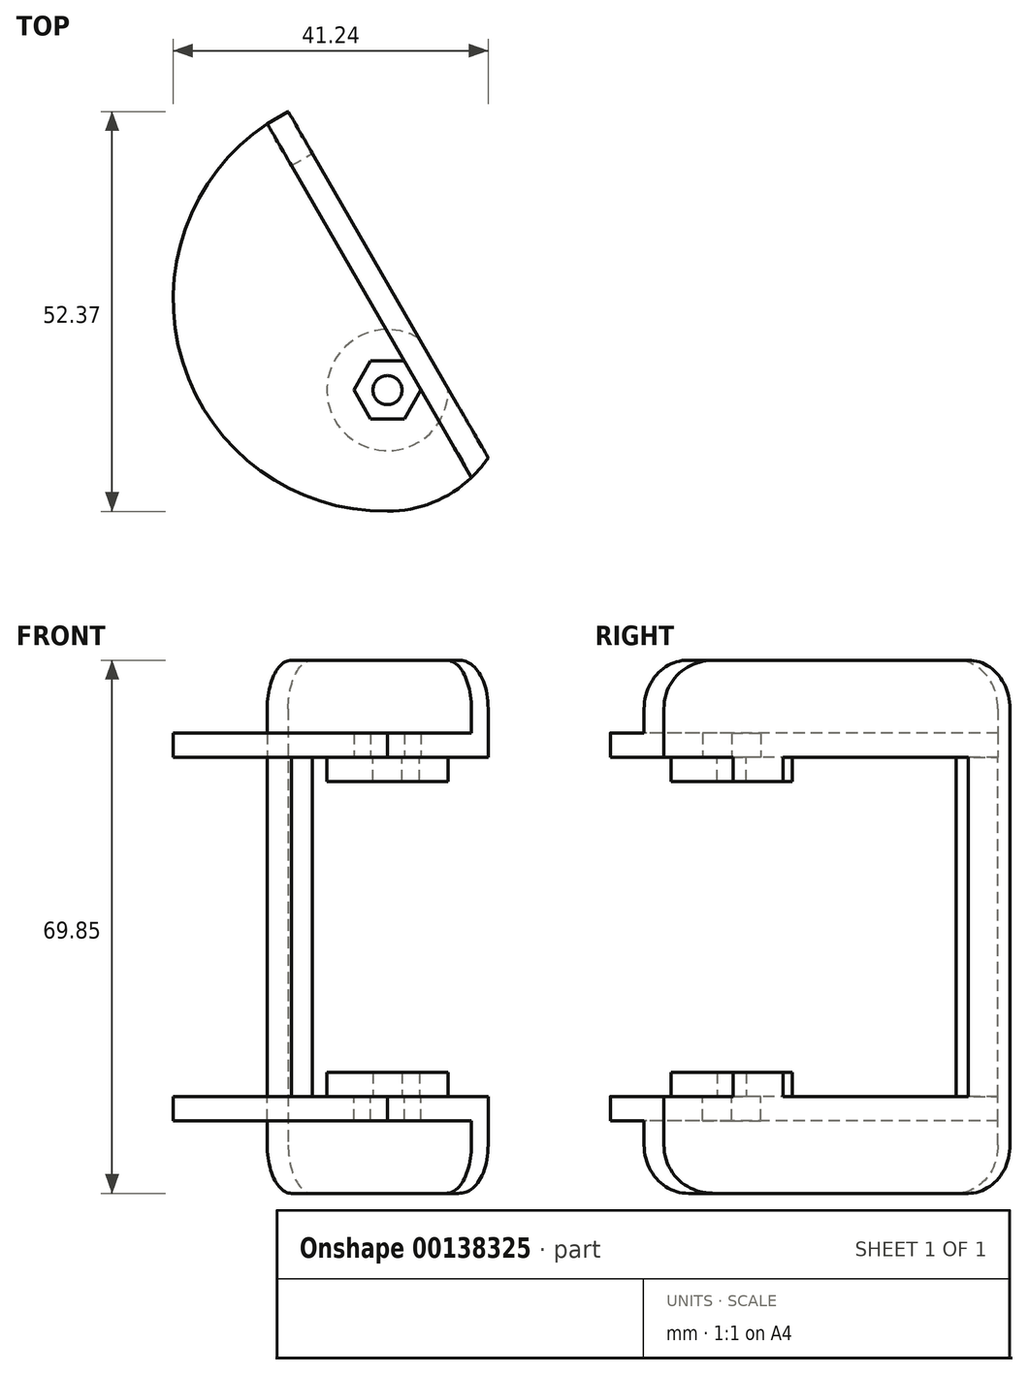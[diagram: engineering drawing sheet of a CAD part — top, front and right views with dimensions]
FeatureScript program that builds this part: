
annotation { "Feature Type Name" : "Feature", "Feature Type Description" : "" }
export const myFeature = defineFeature(function(context is Context, id is Id, definition is map)
    precondition{}
    {
        {
            var Q0;
            Q0=qCreatedBy(makeId("Top.planeOp"),FACE);
            var sketch = newSketch(context, id + "F0", { "sketchPlane" : qUnion([Q0])});
            skArc(sketch, "E0", {"start": v(-4.4, 15.25) * mm, "mid": v(-12.83, -9.36) * mm, "end": v(13.18, -8.85) * mm});
            skPoint(sketch, "E1", {"position": v(0, -15.88) * mm});
            skArc(sketch, "E2", {"start": v(-15.75, 34.9) * mm, "mid": v(-26.82, 3.64) * mm, "end": v(0, -15.88) * mm});
            skCircle(sketch, "E3", {"center": v(0, 0) * mm, "radius": 1.9 * mm});
            skCircle(sketch, "E4.cCircle", {"center": v(0, 0) * mm, "radius": 3.81 * mm, "construction": true});
            skLineSegment(sketch, "E4.0", {"start": v(4.4, 0) * mm, "end": v(2.2, -3.81) * mm});
            skLineSegment(sketch, "E4.1", {"start": v(2.2, -3.81) * mm, "end": v(-2.2, -3.81) * mm});
            skLineSegment(sketch, "E4.2", {"start": v(-2.2, -3.8) * mm, "end": v(-4.4, 0) * mm});
            skLineSegment(sketch, "E4.3", {"start": v(-4.4, 0) * mm, "end": v(-2.2, 3.81) * mm});
            skLineSegment(sketch, "E4.4", {"start": v(-2.2, 3.81) * mm, "end": v(2.2, 3.8) * mm});
            skLineSegment(sketch, "E4.5", {"start": v(2.2, 3.8) * mm, "end": v(4.4, 0) * mm});
            skPoint(sketch, "E4.0.midPoint", {"position": v(3.3, -1.9) * mm});
            skLineSegment(sketch, "E5", {"start": v(11, -11.44) * mm, "end": v(-15.75, 34.9) * mm});
            skLineSegment(sketch, "E6", {"start": v(-15.75, 34.9) * mm, "end": v(-15.75, 34.9) * mm});
            skLineSegment(sketch, "E7", {"start": v(13.18, -8.85) * mm, "end": v(-13, 36.49) * mm});
            skLineSegment(sketch, "E8", {"start": v(-15.75, 34.9) * mm, "end": v(-13, 36.49) * mm});
            skLineSegment(sketch, "E9", {"start": v(-12.58, 29.4) * mm, "end": v(-9.83, 30.99) * mm});
            skArc(sketch, "E10", {"start": v(4.16, 6.76) * mm, "mid": v(-6.87, -3.97) * mm, "end": v(7.93, 0.23) * mm});
            skLineSegment(sketch, "E11", {"start": v(-1.08, 9.5) * mm, "end": v(1.67, 11.08) * mm});
            skSolve(sketch);
        }
        {
            var Q0;
            {var subQ0=sQuery(id+"F0.wireOp",EDGE,"E4.0");Q0=makeQuery(id+"F0.imprint","IMPRINT",FACE,{"disambiguationData":[TD([[makeQuery(id+"F0.imprint","IMPRINT",EDGE,{"derivedFrom":subQ0}),1.0]])]});}
            var Q1;
            {var subQ4=sQuery(id+"F0.wireOp",EDGE,"E5");var subQ5=makeQuery(id+"F0.imprint","INTERSECT",VERTEX,{"derivedFrom":[sQuery(id+"F0.wireOp",EDGE,"E4.0"),subQ4]});Q1=makeQuery(id+"F0.imprint","IMPRINT",FACE,{"disambiguationData":[TD([[makeQuery(id+"F0.imprint","IMPRINT",EDGE,{"disambiguationData":[TD([[subQ5,1.0]])],"derivedFrom":subQ4}),-1.0]])]});}
            var Q2;
            Q2=makeQuery(id+"F0.imprint","IMPRINT",FACE,{"disambiguationData":[TD([[makeQuery(id+"F0.imprint","IMPRINT",EDGE,{"derivedFrom":sQuery(id+"F0.wireOp",EDGE,"E3")}),-1.0]])]});
            extrude(context, id + "F1", {"entities" : qUnion([Q0, Q1, Q2]), "oppositeDirection" : true, "depth" : 3.17 * mm});
        }
        {
            var Q0;
            {var subQ4=sQuery(id+"F0.wireOp",EDGE,"E5");var subQ5=makeQuery(id+"F0.imprint","INTERSECT",VERTEX,{"derivedFrom":[sQuery(id+"F0.wireOp",EDGE,"E4.0"),subQ4]});Q0=makeQuery(id+"F0.imprint","IMPRINT",FACE,{"disambiguationData":[TD([[makeQuery(id+"F0.imprint","IMPRINT",EDGE,{"disambiguationData":[TD([[subQ5,1.0]])],"derivedFrom":subQ4}),-1.0]])]});}
            var Q1;
            {var subQ0=sQuery(id+"F0.wireOp",EDGE,"E7");var subQ1=sQuery(id+"F0.wireOp",EDGE,"E0");var subQ2=makeQuery(id+"F0.imprint","INTERSECT",VERTEX,{"disambiguationData":[OD(1.0)],"derivedFrom":[subQ1,subQ0]});Q1=makeQuery(id+"F0.imprint","IMPRINT",FACE,{"disambiguationData":[TD([[makeQuery(id+"F0.imprint","IMPRINT",EDGE,{"disambiguationData":[TD([[subQ2,1.0]])],"derivedFrom":subQ1}),1.0]])]});}
            var Q2;
            {var subQ1=sQuery(id+"F0.wireOp",EDGE,"E0");var subQ7=makeQuery(id+"F0.imprint","INTERSECT",VERTEX,{"derivedFrom":[subQ1,sQuery(id+"F0.wireOp",EDGE,"E2")]});Q2=makeQuery(id+"F0.imprint","IMPRINT",FACE,{"disambiguationData":[TD([[makeQuery(id+"F0.imprint","IMPRINT",EDGE,{"disambiguationData":[TD([[subQ7,1.0]])],"derivedFrom":subQ1}),1.0]])]});}
            var Q3;
            {var subQ0=sQuery(id+"F0.wireOp",EDGE,"E4.0");Q3=makeQuery(id+"F0.imprint","IMPRINT",FACE,{"disambiguationData":[TD([[makeQuery(id+"F0.imprint","IMPRINT",EDGE,{"derivedFrom":subQ0}),1.0]])]});}
            var Q4;
            {var subQ4=sQuery(id+"F0.wireOp",EDGE,"E2");Q4=makeQuery(id+"F0.imprint","IMPRINT",FACE,{"disambiguationData":[TD([[makeQuery(id+"F0.imprint","IMPRINT",EDGE,{"derivedFrom":subQ4}),1.0]])]});}
            var Q5;
            {var subQ0=sQuery(id+"F0.wireOp",EDGE,"E9");Q5=makeQuery(id+"F0.imprint","IMPRINT",FACE,{"disambiguationData":[TD([[makeQuery(id+"F0.imprint","IMPRINT",EDGE,{"derivedFrom":subQ0}),-1.0]])]});}
            var Q6;
            {var subQ0=sQuery(id+"F0.wireOp",EDGE,"E8");Q6=makeQuery(id+"F0.imprint","IMPRINT",FACE,{"disambiguationData":[TD([[makeQuery(id+"F0.imprint","IMPRINT",EDGE,{"derivedFrom":subQ0}),-1.0]])]});}
            var Q7;
            {var subQ0=sQuery(id+"F0.wireOp",EDGE,"E11");Q7=makeQuery(id+"F0.imprint","IMPRINT",FACE,{"disambiguationData":[TD([[makeQuery(id+"F0.imprint","IMPRINT",EDGE,{"derivedFrom":subQ0}),-1.0]])]});}
            extrude(context, id + "F2", {"entities" : qUnion([Q0, Q1, Q2, Q3, Q4, Q5, Q6, Q7]), "operationType" : NewBodyOperationType.ADD, "depth" : 3.17 * mm});
        }
        {
            var Q0;
            {var subQ0=sQuery(id+"F0.wireOp",EDGE,"E7");var subQ1=sQuery(id+"F0.wireOp",EDGE,"E0");var subQ2=makeQuery(id+"F0.imprint","INTERSECT",VERTEX,{"derivedFrom":[subQ1,subQ0]});Q0=makeQuery(id+"F0.imprint","IMPRINT",FACE,{"disambiguationData":[TD([[makeQuery(id+"F0.imprint","IMPRINT",EDGE,{"disambiguationData":[TD([[subQ2,1.0]])],"derivedFrom":subQ1}),1.0]])]});}
            var Q1;
            {var subQ0=sQuery(id+"F0.wireOp",EDGE,"E11");Q1=makeQuery(id+"F0.imprint","IMPRINT",FACE,{"disambiguationData":[TD([[makeQuery(id+"F0.imprint","IMPRINT",EDGE,{"derivedFrom":subQ0}),-1.0]])]});}
            var Q2;
            {var subQ0=sQuery(id+"F0.wireOp",EDGE,"E9");Q2=makeQuery(id+"F0.imprint","IMPRINT",FACE,{"disambiguationData":[TD([[makeQuery(id+"F0.imprint","IMPRINT",EDGE,{"derivedFrom":subQ0}),-1.0]])]});}
            var Q3;
            {var subQ0=sQuery(id+"F0.wireOp",EDGE,"E8");Q3=makeQuery(id+"F0.imprint","IMPRINT",FACE,{"disambiguationData":[TD([[makeQuery(id+"F0.imprint","IMPRINT",EDGE,{"derivedFrom":subQ0}),-1.0]])]});}
            extrude(context, id + "F3", {"entities" : qUnion([Q0, Q1, Q2, Q3]), "operationType" : NewBodyOperationType.ADD, "depth" : 12.7 * mm});
        }
        {
            var Q0;
            Q0=makeQuery(id+"F2.opExtrude","CAP_FACE",FACE,{"disambiguationData":[OSD([sQuery(id+"F0.wireOp",EDGE,"E0"),sQuery(id+"F0.wireOp",EDGE,"E2"),sQuery(id+"F0.wireOp",EDGE,"E4.0"),sQuery(id+"F0.wireOp",EDGE,"E4.1"),sQuery(id+"F0.wireOp",EDGE,"E4.2"),sQuery(id+"F0.wireOp",EDGE,"E4.3"),sQuery(id+"F0.wireOp",EDGE,"E4.4"),sQuery(id+"F0.wireOp",EDGE,"E5"),sQuery(id+"F0.wireOp",EDGE,"E7"),sQuery(id+"F0.wireOp",EDGE,"E8")])],"isStart":false});
            var sketch = newSketch(context, id + "F4", { "sketchPlane" : qUnion([Q0])});
            skLineSegment(sketch, "E12.0", {"start": v(11, -11.44) * mm, "end": v(-15.75, 34.9) * mm});
            skSolve(sketch);
        }
        {
            var Q0;
            {var subQ0=sQuery(id+"F0.wireOp",EDGE,"E7");Q0=makeQuery(id+"F4.imprint","IMPRINT",FACE,{"disambiguationData":[TD([[makeQuery(id+"F4.imprint","IMPRINT",EDGE,{"derivedFrom":makeQuery(id+"F2.opExtrude","CAP_EDGE",EDGE,{"disambiguationData":[OSD([subQ0])],"isStart":false})}),1.0]])]});}
            extrude(context, id + "F5", {"entities" : qUnion([Q0]), "operationType" : NewBodyOperationType.ADD, "depth" : 9.52 * mm});
        }
        {
            var Q0;
            Q0=makeQuery(id+"F3.opExtrude","CAP_EDGE",EDGE,{"disambiguationData":[OSD([sQuery(id+"F0.wireOp",EDGE,"E8")])],"isStart":false});
            var Q1;
            Q1=makeQuery(id+"F3.opExtrude","CAP_EDGE",EDGE,{"disambiguationData":[OSD([sQuery(id+"F0.wireOp",EDGE,"E0")])],"isStart":false});
            fillet(context, id + "F6", {"entities" : qUnion([Q0, Q1]), "radius" : 6.35 * mm, "tangentPropagation" : true, "allowEdgeOverflow" : false});
        }
        {
            var Q0;
            Q0=makeQuery(id+"F1.opExtrude","CAP_FACE",FACE,{"disambiguationData":[OSD([sQuery(id+"F0.wireOp",EDGE,"E3"),sQuery(id+"F0.wireOp",EDGE,"E7"),sQuery(id+"F0.wireOp",EDGE,"E10")])],"isStart":false});
            cPlane(context, id + "F7", {"entities" : qUnion([Q0]), "cplaneType" : CPlaneType.OFFSET, "offset" : 19.05 * mm, "width" : 152.4 * mm, "height" : 152.4 * mm});
        }
        {
            var Q0;
            Q0=makeQuery(id+"F1.opExtrude","SWEPT_BODY",BODY,{"disambiguationData":[OSD([sQuery(id+"F0.wireOp",EDGE,"E3"),sQuery(id+"F0.wireOp",EDGE,"E7"),sQuery(id+"F0.wireOp",EDGE,"E10")])]});
            var Q1;
            Q1=qCreatedBy(id+"F7.planeOp",FACE);
            mirror(context, id + "F8", {"entities" : qUnion([Q0]), "mirrorPlane" : qUnion([Q1])});
        }
        {
            var Q0;
            {var subQ0=sQuery(id+"F0.wireOp",EDGE,"E8");Q0=makeQuery(id+"F0.imprint","IMPRINT",FACE,{"disambiguationData":[TD([[makeQuery(id+"F0.imprint","IMPRINT",EDGE,{"derivedFrom":subQ0}),-1.0]])]});}
            extrude(context, id + "F9", {"entities" : qUnion([Q0]), "operationType" : NewBodyOperationType.ADD, "endBound" : BoundingType.UP_TO_NEXT, "oppositeDirection" : true, "depth" : 25.4 * mm});
        }
    });
